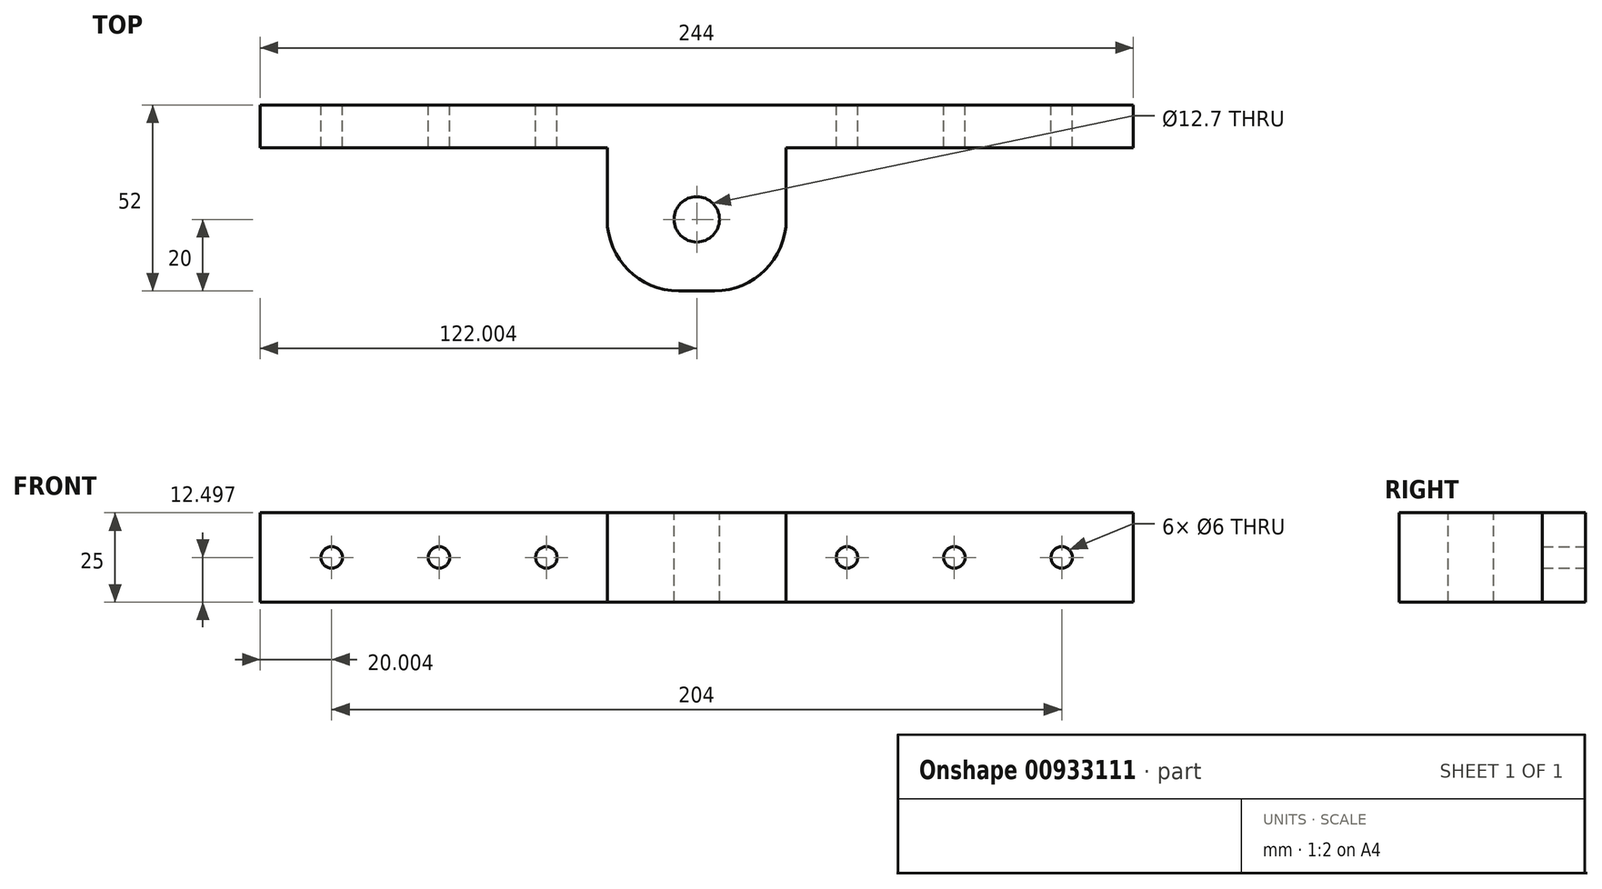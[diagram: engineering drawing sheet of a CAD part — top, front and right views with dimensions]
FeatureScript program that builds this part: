
annotation { "Feature Type Name" : "Feature", "Feature Type Description" : "" }
export const myFeature = defineFeature(function(context is Context, id is Id, definition is map)
    precondition{}
    {
        {
            var Q0;
            Q0=qCreatedBy(makeId("Front.planeOp"),FACE);
            var sketch = newSketch(context, id + "F0", { "sketchPlane" : qUnion([Q0])});
            skLineSegment(sketch, "E0.bottom", {"start": v(-107.58, 0.48) * mm, "end": v(136.42, 0.48) * mm});
            skLineSegment(sketch, "E0.top", {"start": v(-107.58, -24.52) * mm, "end": v(136.42, -24.52) * mm});
            skLineSegment(sketch, "E0.left", {"start": v(-107.58, 0.48) * mm, "end": v(-107.58, -24.52) * mm});
            skLineSegment(sketch, "E0.right", {"start": v(136.42, 0.48) * mm, "end": v(136.42, -24.52) * mm});
            skSolve(sketch);
        }
        {
            var Q0;
            Q0 = qSketchRegion(id + "F0", true);
            extrude(context, id + "F1", {"entities" : qUnion([Q0]), "depth" : 12 * mm, "offsetDistance" : 25 * mm});
        }
        {
            var Q0;
            Q0=makeQuery(id+"F1.opExtrude","CAP_FACE",FACE,{"disambiguationData":[OSD([sQuery(id+"F0.wireOp",EDGE,"E0.bottom"),sQuery(id+"F0.wireOp",EDGE,"E0.top"),sQuery(id+"F0.wireOp",EDGE,"E0.left"),sQuery(id+"F0.wireOp",EDGE,"E0.right")])],"isStart":false});
            var sketch = newSketch(context, id + "F2", { "sketchPlane" : qUnion([Q0])});
            skLineSegment(sketch, "E1.bottom", {"start": v(-10.58, 0.48) * mm, "end": v(39.42, 0.48) * mm});
            skLineSegment(sketch, "E1.top", {"start": v(-10.58, -24.52) * mm, "end": v(39.42, -24.52) * mm});
            skLineSegment(sketch, "E1.left", {"start": v(-10.58, 0.48) * mm, "end": v(-10.58, -24.52) * mm});
            skLineSegment(sketch, "E1.right", {"start": v(39.42, 0.48) * mm, "end": v(39.42, -24.52) * mm});
            skPoint(sketch, "E2", {"position": v(14.42, 0.48) * mm});
            skPoint(sketch, "E3", {"position": v(14.42, -24.52) * mm});
            skSolve(sketch);
        }
        {
            var Q0;
            Q0=makeQuery(id+"F2.imprint","IMPRINT",FACE,{"disambiguationData":[TD([[makeQuery(id+"F2.imprint","IMPRINT",EDGE,{"derivedFrom":sQuery(id+"F2.wireOp",EDGE,"E1.bottom")}),-1.0]])]});
            extrude(context, id + "F3", {"entities" : qUnion([Q0]), "operationType" : NewBodyOperationType.ADD, "depth" : 40 * mm, "offsetDistance" : 25 * mm});
        }
        {
            var Q0;
            Q0=makeQuery(id+"F3.boolean.opBoolean","MERGE",FACE,{"derivedFrom":[makeQuery(id+"FuKEyyl3DLeD4mr_1.boolean.opBoolean","MERGE",FACE,{"derivedFrom":[makeQuery(id+"F1.opExtrude","SWEPT_FACE",FACE,{"disambiguationData":[OSD([sQuery(id+"F0.wireOp",EDGE,"E0.bottom")])]}),makeQuery(id+"FuKEyyl3DLeD4mr_1.opExtrude","SWEPT_FACE",FACE,{"disambiguationData":[OSD([sQuery(id+"FIb6bImb8Af4elt_1.wireOp",EDGE,"2ulOIIcz-b08C-mDPE-Q4UN-79ysGMYGsBvn.bottom")])]}),makeQuery(id+"FuKEyyl3DLeD4mr_1.opExtrude","SWEPT_FACE",FACE,{"disambiguationData":[OSD([sQuery(id+"FIb6bImb8Af4elt_1.wireOp",EDGE,"Pv7EgeaX-UQBh-VlCa-RkTk-jYxMJ4lPvPS8.bottom")])]})]}),makeQuery(id+"F3.opExtrude","SWEPT_FACE",FACE,{"disambiguationData":[OSD([sQuery(id+"F2.wireOp",EDGE,"E1.bottom")])]})]});
            var sketch = newSketch(context, id + "F4", { "sketchPlane" : qUnion([Q0])});
            skLineSegment(sketch, "E4", {"start": v(14.42, -52) * mm, "end": v(14.42, 0) * mm, "construction": true});
            skLineSegment(sketch, "E5", {"start": v(-10.58, -32) * mm, "end": v(14.42, -32) * mm, "construction": true});
            skPoint(sketch, "E6.orphan", {"position": v(39.42, -32) * mm});
            skCircle(sketch, "E7", {"center": v(14.42, -32) * mm, "radius": 6.35 * mm});
            skSolve(sketch);
        }
        {
            var Q0;
            Q0 = qSketchRegion(id + "F4", true);
            extrude(context, id + "F5", {"entities" : qUnion([Q0]), "operationType" : NewBodyOperationType.REMOVE, "endBound" : BoundingType.THROUGH_ALL, "oppositeDirection" : true, "depth" : 25 * mm, "offsetDistance" : 25 * mm});
        }
        {
            var Q0;
            Q0=makeQuery(id+"F3.opExtrude","CAP_EDGE",EDGE,{"disambiguationData":[OSD([sQuery(id+"F2.wireOp",EDGE,"E1.left")])],"isStart":false});
            fillet(context, id + "F6", {"entities" : qUnion([Q0]), "radius" : 20 * mm, "tangentPropagation" : true, "allowEdgeOverflow" : false});
        }
        {
            var Q0;
            Q0=makeQuery(id+"F3.opExtrude","CAP_EDGE",EDGE,{"disambiguationData":[OSD([sQuery(id+"F2.wireOp",EDGE,"E1.right")])],"isStart":false});
            fillet(context, id + "F7", {"entities" : qUnion([Q0]), "radius" : 20 * mm, "tangentPropagation" : true, "allowEdgeOverflow" : false});
        }
        {
            var Q0;
            Q0=makeQuery(id+"F1.opExtrude","CAP_FACE",FACE,{"disambiguationData":[OSD([sQuery(id+"F0.wireOp",EDGE,"E0.bottom"),sQuery(id+"F0.wireOp",EDGE,"E0.top"),sQuery(id+"F0.wireOp",EDGE,"E0.left"),sQuery(id+"F0.wireOp",EDGE,"E0.right")])],"isStart":true});
            var sketch = newSketch(context, id + "F8", { "sketchPlane" : qUnion([Q0])});
            skLineSegment(sketch, "E8", {"start": v(-136.42, -12.02) * mm, "end": v(107.58, -12.02) * mm, "construction": true});
            skCircle(sketch, "E9", {"center": v(87.58, -12.02) * mm, "radius": 3 * mm});
            skCircle(sketch, "E10", {"center": v(57.58, -12.02) * mm, "radius": 3 * mm});
            skCircle(sketch, "E11", {"center": v(-86.42, -12.02) * mm, "radius": 3 * mm});
            skCircle(sketch, "E12", {"center": v(-116.42, -12.02) * mm, "radius": 3 * mm});
            skCircle(sketch, "E13", {"center": v(-56.42, -12.02) * mm, "radius": 3 * mm});
            skCircle(sketch, "E14", {"center": v(27.58, -12.02) * mm, "radius": 3 * mm});
            skSolve(sketch);
        }
        {
            var Q0;
            Q0 = qSketchRegion(id + "F8", true);
            extrude(context, id + "F9", {"entities" : qUnion([Q0]), "operationType" : NewBodyOperationType.REMOVE, "endBound" : BoundingType.THROUGH_ALL, "oppositeDirection" : true, "depth" : 25 * mm, "offsetDistance" : 25 * mm});
        }
    });
